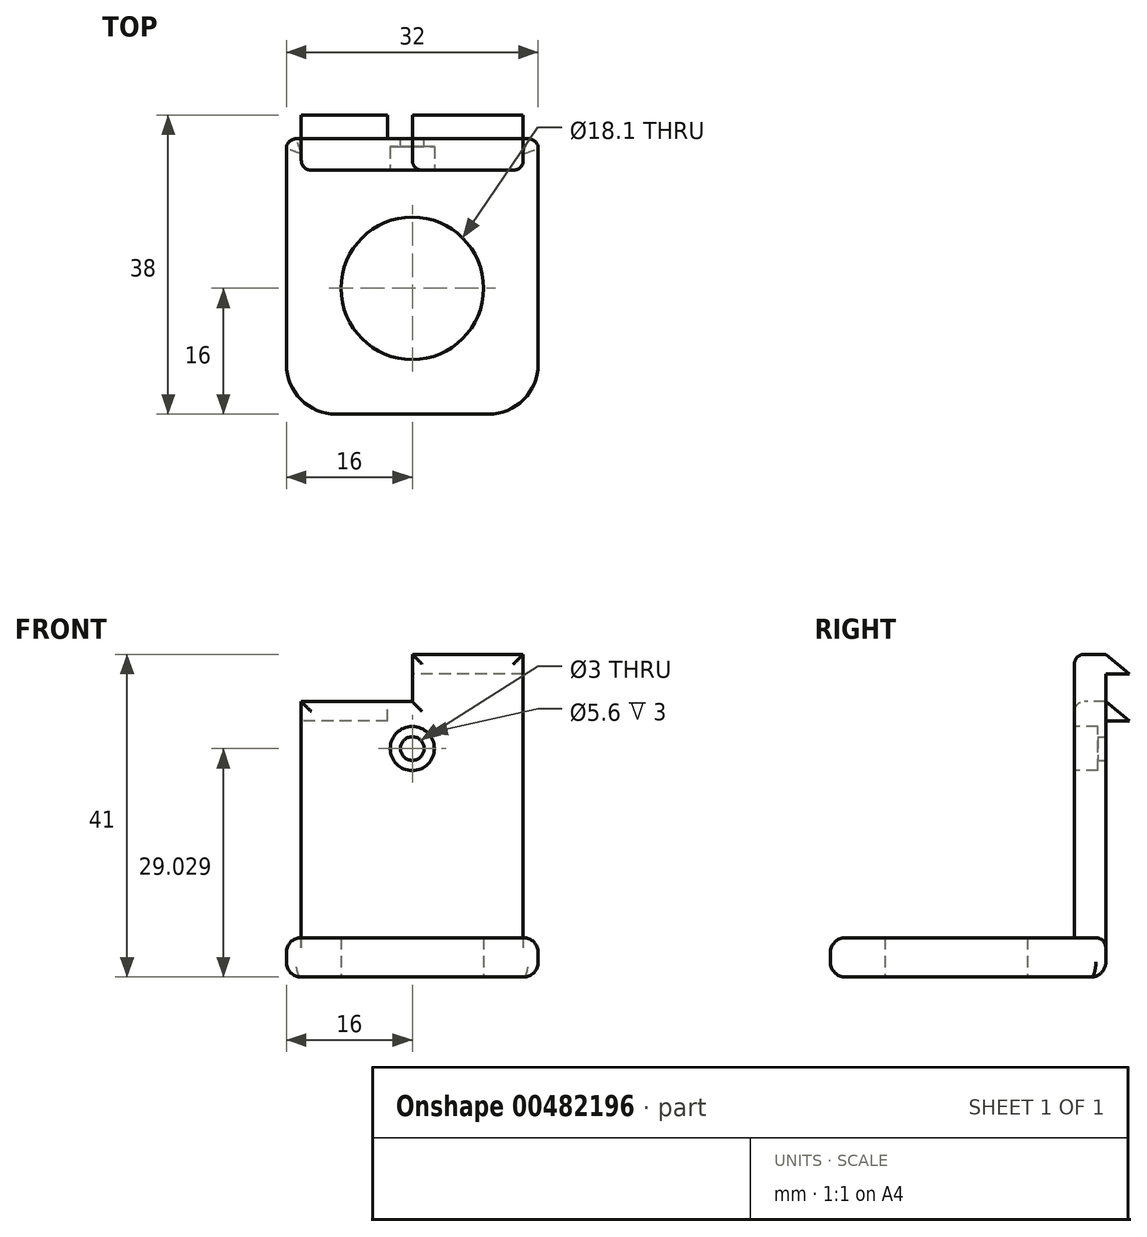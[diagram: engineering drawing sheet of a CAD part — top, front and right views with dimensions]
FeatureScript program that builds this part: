
annotation { "Feature Type Name" : "Feature", "Feature Type Description" : "" }
export const myFeature = defineFeature(function(context is Context, id is Id, definition is map)
    precondition{}
    {
        {
            var Q0;
            Q0=qCreatedBy(makeId("Top.planeOp"),FACE);
            var sketch = newSketch(context, id + "F0", { "sketchPlane" : qUnion([Q0])});
            skCircle(sketch, "E0", {"center": v(0, 0) * mm, "radius": 9.05 * mm});
            skLineSegment(sketch, "E1.bottom", {"start": v(-16, 19) * mm, "end": v(16, 19) * mm});
            skLineSegment(sketch, "E1.top", {"start": v(-9.65, -16) * mm, "end": v(9.65, -16) * mm});
            skLineSegment(sketch, "E1.left", {"start": v(-16, 19) * mm, "end": v(-16, -9.65) * mm});
            skLineSegment(sketch, "E1.right", {"start": v(16, 19) * mm, "end": v(16, -9.65) * mm});
            skPoint(sketch, "E2.visualSharp", {"position": v(-16, -16) * mm});
            skArc(sketch, "E2.filletArc", {"start": v(-16, -9.65) * mm, "mid": v(-14.14, -14.14) * mm, "end": v(-9.65, -16) * mm});
            skPoint(sketch, "E3.visualSharp", {"position": v(16, -16) * mm});
            skArc(sketch, "E3.filletArc", {"start": v(9.65, -16) * mm, "mid": v(14.14, -14.14) * mm, "end": v(16, -9.65) * mm});
            skSolve(sketch);
        }
        {
            var Q0;
            Q0=makeQuery(id+"F0.imprint","IMPRINT",FACE,{"disambiguationData":[TD([[makeQuery(id+"F0.imprint","IMPRINT",EDGE,{"derivedFrom":sQuery(id+"F0.wireOp",EDGE,"E0")}),-1.0]])]});
            extrude(context, id + "F1", {"entities" : qUnion([Q0]), "depth" : 5 * mm});
        }
        {
            var Q0;
            Q0=makeQuery(id+"F1.opExtrude","CAP_EDGE",EDGE,{"disambiguationData":[OSD([sQuery(id+"F0.wireOp",EDGE,"E1.bottom")])],"isStart":true});
            var Q1;
            Q1=makeQuery(id+"F1.opExtrude","CAP_EDGE",EDGE,{"disambiguationData":[OSD([sQuery(id+"F0.wireOp",EDGE,"E1.right")])],"isStart":true});
            fillet(context, id + "F2", {"entities" : qUnion([Q0, Q1]), "radius" : 1.9 * mm, "tangentPropagation" : true, "allowEdgeOverflow" : false});
        }
        {
            var Q0;
            Q0=makeQuery(id+"F1.opExtrude","CAP_EDGE",EDGE,{"disambiguationData":[OSD([sQuery(id+"F0.wireOp",EDGE,"E1.top")])],"isStart":false});
            var Q1;
            Q1=makeQuery(id+"F1.opExtrude","CAP_EDGE",EDGE,{"disambiguationData":[OSD([sQuery(id+"F0.wireOp",EDGE,"E1.right")])],"isStart":false});
            fillet(context, id + "F3", {"entities" : qUnion([Q0, Q1]), "radius" : 1.9 * mm, "tangentPropagation" : true, "allowEdgeOverflow" : false});
        }
        {
            var Q0;
            Q0=makeQuery(id+"F1.opExtrude","CAP_FACE",FACE,{"disambiguationData":[OSD([sQuery(id+"F0.wireOp",EDGE,"E0"),sQuery(id+"F0.wireOp",EDGE,"E1.bottom"),sQuery(id+"F0.wireOp",EDGE,"E1.top"),sQuery(id+"F0.wireOp",EDGE,"E1.left"),sQuery(id+"F0.wireOp",EDGE,"E1.right"),sQuery(id+"F0.wireOp",EDGE,"E2.filletArc"),sQuery(id+"F0.wireOp",EDGE,"E3.filletArc")])],"isStart":false});
            var sketch = newSketch(context, id + "F4", { "sketchPlane" : qUnion([Q0])});
            skLineSegment(sketch, "E4.bottom", {"start": v(-14.1, 19) * mm, "end": v(14.1, 19) * mm});
            skLineSegment(sketch, "E4.top", {"start": v(-14.1, 15) * mm, "end": v(14.1, 15) * mm});
            skLineSegment(sketch, "E4.left", {"start": v(-14.1, 19) * mm, "end": v(-14.1, 15) * mm});
            skLineSegment(sketch, "E4.right", {"start": v(14.1, 19) * mm, "end": v(14.1, 15) * mm});
            skSolve(sketch);
        }
        {
            var Q0;
            Q0=makeQuery(id+"F4.imprint","IMPRINT",FACE,{"disambiguationData":[TD([[makeQuery(id+"F4.imprint","IMPRINT",EDGE,{"derivedFrom":sQuery(id+"F4.wireOp",EDGE,"E4.bottom")}),-1.0]])]});
            extrude(context, id + "F5", {"entities" : qUnion([Q0]), "operationType" : NewBodyOperationType.ADD, "depth" : 30 * mm});
        }
        {
            var Q0;
            Q0=qCreatedBy(makeId("Right.planeOp"),FACE);
            var sketch = newSketch(context, id + "F6", { "sketchPlane" : qUnion([Q0])});
            skLineSegment(sketch, "E5", {"start": v(19, 35) * mm, "end": v(19, 32.53) * mm});
            skLineSegment(sketch, "E6", {"start": v(19, 32.53) * mm, "end": v(22, 32.53) * mm});
            skLineSegment(sketch, "E7", {"start": v(22, 32.53) * mm, "end": v(19, 35) * mm});
            skSolve(sketch);
        }
        {
            var Q0;
            Q0=makeQuery(id+"F6.imprint","IMPRINT",FACE,{"disambiguationData":[TD([[makeQuery(id+"F6.imprint","IMPRINT",EDGE,{"derivedFrom":sQuery(id+"F6.wireOp",EDGE,"E5")}),1.0]])]});
            var Q1;
            Q1=makeQuery(id+"F5.opExtrude","SWEPT_FACE",FACE,{"disambiguationData":[OSD([sQuery(id+"F4.wireOp",EDGE,"E4.right")])]});
            var Q2;
            Q2=makeQuery(id+"F5.opExtrude","SWEPT_FACE",FACE,{"disambiguationData":[OSD([sQuery(id+"F4.wireOp",EDGE,"E4.left")])]});
            extrude(context, id + "F7", {"entities" : qUnion([Q0]), "operationType" : NewBodyOperationType.ADD, "endBound" : BoundingType.UP_TO_SURFACE, "endBoundEntityFace" : qUnion([Q1]), "depth" : 25.4 * mm, "hasSecondDirection" : true, "secondDirectionBound" : SecondDirectionBoundingType.UP_TO_SURFACE, "secondDirectionOppositeDirection" : true, "secondDirectionBoundEntityFace" : qUnion([Q2]), "secondDirectionDepth" : 25.4 * mm});
        }
        {
            var Q0;
            Q0=makeQuery(id+"F5.boolean.opBoolean","MERGE",FACE,{"derivedFrom":[makeQuery(id+"F1.opExtrude","SWEPT_FACE",FACE,{"disambiguationData":[OSD([sQuery(id+"F0.wireOp",EDGE,"E1.bottom")])]}),makeQuery(id+"F5.opExtrude","SWEPT_FACE",FACE,{"disambiguationData":[OSD([sQuery(id+"F4.wireOp",EDGE,"E4.bottom")])]})]});
            var sketch = newSketch(context, id + "F8", { "sketchPlane" : qUnion([Q0])});
            skCircle(sketch, "E8", {"center": v(0, 29.03) * mm, "radius": 1.5 * mm});
            skSolve(sketch);
        }
        {
            var Q0;
            Q0=makeQuery(id+"F8.imprint","IMPRINT",FACE,{"disambiguationData":[TD([[makeQuery(id+"F8.imprint","IMPRINT",EDGE,{"derivedFrom":sQuery(id+"F8.wireOp",EDGE,"E8")}),1.0]])]});
            var Q1;
            Q1=makeQuery(id+"F5.opExtrude","SWEPT_FACE",FACE,{"disambiguationData":[OSD([sQuery(id+"F4.wireOp",EDGE,"E4.top")])]});
            extrude(context, id + "F9", {"entities" : qUnion([Q0]), "operationType" : NewBodyOperationType.REMOVE, "endBound" : BoundingType.UP_TO_SURFACE, "oppositeDirection" : true, "endBoundEntityFace" : qUnion([Q1]), "depth" : 25.4 * mm});
        }
        {
            var Q0;
            Q0=makeQuery(id+"F5.opExtrude","SWEPT_FACE",FACE,{"disambiguationData":[OSD([sQuery(id+"F4.wireOp",EDGE,"E4.top")])]});
            var sketch = newSketch(context, id + "F10", { "sketchPlane" : qUnion([Q0])});
            skCircle(sketch, "E9", {"center": v(0, 29.03) * mm, "radius": 2.8 * mm});
            skSolve(sketch);
        }
        {
            var Q0;
            Q0=makeQuery(id+"F10.imprint","IMPRINT",FACE,{"disambiguationData":[TD([[makeQuery(id+"F10.imprint","IMPRINT",EDGE,{"derivedFrom":sQuery(id+"F10.wireOp",EDGE,"E9")}),1.0]])]});
            extrude(context, id + "F11", {"entities" : qUnion([Q0]), "operationType" : NewBodyOperationType.REMOVE, "oppositeDirection" : true, "depth" : 3 * mm});
        }
        {
            var Q0;
            Q0=qCreatedBy(makeId("Right.planeOp"),FACE);
            var sketch = newSketch(context, id + "F12", { "sketchPlane" : qUnion([Q0])});
            skLineSegment(sketch, "E10", {"start": v(19, 30.98) * mm, "end": v(19, 35) * mm});
            skLineSegment(sketch, "E11", {"start": v(19, 35) * mm, "end": v(23.3, 32.12) * mm});
            skLineSegment(sketch, "E12", {"start": v(23.3, 32.12) * mm, "end": v(19, 30.98) * mm});
            skSolve(sketch);
        }
        {
            var Q0;
            Q0=makeQuery(id+"F12.imprint","IMPRINT",FACE,{"disambiguationData":[TD([[makeQuery(id+"F12.imprint","IMPRINT",EDGE,{"derivedFrom":sQuery(id+"F12.wireOp",EDGE,"E10")}),-1.0]])]});
            extrude(context, id + "F13", {"entities" : qUnion([Q0]), "operationType" : NewBodyOperationType.REMOVE, "depth" : 14.82 * mm, "hasSecondDirection" : true, "secondDirectionOppositeDirection" : true, "secondDirectionDepth" : 3.12 * mm});
        }
        {
            var Q0;
            Q0=makeQuery(id+"F5.opExtrude","CAP_FACE",FACE,{"disambiguationData":[OSD([sQuery(id+"F4.wireOp",EDGE,"E4.bottom"),sQuery(id+"F4.wireOp",EDGE,"E4.top"),sQuery(id+"F4.wireOp",EDGE,"E4.left"),sQuery(id+"F4.wireOp",EDGE,"E4.right")])],"isStart":false});
            var sketch = newSketch(context, id + "F14", { "sketchPlane" : qUnion([Q0])});
            skLineSegment(sketch, "E13.bottom", {"start": v(0, 19) * mm, "end": v(14.1, 19) * mm});
            skLineSegment(sketch, "E13.top", {"start": v(0, 15) * mm, "end": v(14.1, 15) * mm});
            skLineSegment(sketch, "E13.left", {"start": v(0, 19) * mm, "end": v(0, 15) * mm});
            skLineSegment(sketch, "E13.right", {"start": v(14.1, 19) * mm, "end": v(14.1, 15) * mm});
            skSolve(sketch);
        }
        {
            var Q0;
            Q0=qSketchRegion(id+"F14",true);
            extrude(context, id + "F15", {"entities" : qUnion([Q0]), "operationType" : NewBodyOperationType.ADD, "depth" : 6 * mm});
        }
        {
            var Q0;
            Q0=qCreatedBy(makeId("Right.planeOp"),FACE);
            var sketch = newSketch(context, id + "F16", { "sketchPlane" : qUnion([Q0])});
            skLineSegment(sketch, "E14", {"start": v(19, 41) * mm, "end": v(22, 38.53) * mm});
            skLineSegment(sketch, "E15", {"start": v(22, 38.53) * mm, "end": v(19, 38.53) * mm});
            skLineSegment(sketch, "E16", {"start": v(19, 38.53) * mm, "end": v(19, 41) * mm});
            skSolve(sketch);
        }
        {
            var Q0;
            Q0=makeQuery(id+"F16.imprint","IMPRINT",FACE,{"disambiguationData":[TD([[makeQuery(id+"F16.imprint","IMPRINT",EDGE,{"derivedFrom":sQuery(id+"F16.wireOp",EDGE,"E14")}),-1.0]])]});
            var Q1;
            Q1=makeQuery(id+"F15.boolean.opBoolean","MERGE",FACE,{"derivedFrom":[makeQuery(id+"F7.boolean.opBoolean","MERGE",FACE,{"derivedFrom":[makeQuery(id+"F5.opExtrude","SWEPT_FACE",FACE,{"disambiguationData":[OSD([sQuery(id+"F4.wireOp",EDGE,"E4.right")])]}),makeQuery(id+"F7.opExtrude","CAP_FACE",FACE,{"disambiguationData":[OSD([sQuery(id+"F6.wireOp",EDGE,"E5"),sQuery(id+"F6.wireOp",EDGE,"E6"),sQuery(id+"F6.wireOp",EDGE,"E7")])],"isStart":false})]}),makeQuery(id+"F15.opExtrude","SWEPT_FACE",FACE,{"disambiguationData":[OSD([sQuery(id+"F14.wireOp",EDGE,"E13.right")])]})]});
            extrude(context, id + "F17", {"entities" : qUnion([Q0]), "operationType" : NewBodyOperationType.ADD, "endBound" : BoundingType.UP_TO_SURFACE, "endBoundEntityFace" : qUnion([Q1]), "depth" : 25.4 * mm});
        }
        {
            var Q0;
            Q0=makeQuery(id+"F5.opExtrude","SWEPT_EDGE",EDGE,{"disambiguationData":[OSD([sQuery(id+"F0.wireOp",EDGE,"E0"),sQuery(id+"F0.wireOp",EDGE,"E1.bottom"),sQuery(id+"F0.wireOp",EDGE,"E1.top"),sQuery(id+"F0.wireOp",EDGE,"E1.left"),sQuery(id+"F0.wireOp",EDGE,"E1.right"),sQuery(id+"F0.wireOp",EDGE,"E2.filletArc"),sQuery(id+"F0.wireOp",EDGE,"E3.filletArc"),sQuery(id+"F4.wireOp",EDGE,"E4.top"),sQuery(id+"F4.wireOp",EDGE,"E4.right")])]});
            var Q1;
            Q1=makeQuery(id+"F15.boolean.opBoolean","MERGE",EDGE,{"derivedFrom":[makeQuery(id+"F5.opExtrude","SWEPT_EDGE",EDGE,{"disambiguationData":[OSD([sQuery(id+"F0.wireOp",EDGE,"E0"),sQuery(id+"F0.wireOp",EDGE,"E1.bottom"),sQuery(id+"F0.wireOp",EDGE,"E1.top"),sQuery(id+"F0.wireOp",EDGE,"E1.left"),sQuery(id+"F0.wireOp",EDGE,"E1.right"),sQuery(id+"F0.wireOp",EDGE,"E2.filletArc"),sQuery(id+"F0.wireOp",EDGE,"E3.filletArc"),sQuery(id+"F4.wireOp",EDGE,"E4.top"),sQuery(id+"F4.wireOp",EDGE,"E4.left")])]}),makeQuery(id+"F15.opExtrude","SWEPT_EDGE",EDGE,{"disambiguationData":[OSD([sQuery(id+"F14.wireOp",EDGE,"9835426e-c448-4567-998b-7149fbf15287.bottom"),sQuery(id+"F14.wireOp",EDGE,"9835426e-c448-4567-998b-7149fbf15287.right")])]})]});
            var Q2;
            Q2=makeQuery(id+"F15.opExtrude","CAP_EDGE",EDGE,{"disambiguationData":[OSD([sQuery(id+"F14.wireOp",EDGE,"9835426e-c448-4567-998b-7149fbf15287.bottom")])],"isStart":false});
            var Q3;
            Q3=makeQuery(id+"F5.opExtrude","CAP_EDGE",EDGE,{"disambiguationData":[OSD([sQuery(id+"F4.wireOp",EDGE,"E4.top")])],"isStart":false});
            var Q4;
            Q4=makeQuery(id+"F15.opExtrude","SWEPT_EDGE",EDGE,{"disambiguationData":[OSD([sQuery(id+"F4.wireOp",EDGE,"E4.top"),sQuery(id+"F14.wireOp",EDGE,"9835426e-c448-4567-998b-7149fbf15287.bottom"),sQuery(id+"F14.wireOp",EDGE,"9835426e-c448-4567-998b-7149fbf15287.right")])]});
            var Q5;
            Q5=makeQuery(id+"F5.opExtrude","SWEPT_EDGE",EDGE,{"disambiguationData":[OSD([sQuery(id+"F0.wireOp",EDGE,"E0"),sQuery(id+"F0.wireOp",EDGE,"E1.bottom"),sQuery(id+"F0.wireOp",EDGE,"E1.top"),sQuery(id+"F0.wireOp",EDGE,"E1.left"),sQuery(id+"F0.wireOp",EDGE,"E1.right"),sQuery(id+"F0.wireOp",EDGE,"E2.filletArc"),sQuery(id+"F0.wireOp",EDGE,"E3.filletArc"),sQuery(id+"F4.wireOp",EDGE,"E4.top"),sQuery(id+"F4.wireOp",EDGE,"E4.left")])]});
            var Q6;
            Q6=makeQuery(id+"F15.opExtrude","CAP_EDGE",EDGE,{"disambiguationData":[OSD([sQuery(id+"F14.wireOp",EDGE,"E13.top")])],"isStart":false});
            fillet(context, id + "F18", {"entities" : qUnion([Q0, Q1, Q2, Q3, Q4, Q5, Q6]), "radius" : 1.27 * mm, "tangentPropagation" : true, "allowEdgeOverflow" : false});
        }
        {
            var Q0;
            Q0=makeQuery(id+"F1.opExtrude","SWEPT_EDGE",EDGE,{"disambiguationData":[OSD([sQuery(id+"F0.wireOp",EDGE,"E1.bottom"),sQuery(id+"F0.wireOp",EDGE,"E1.left")])]});
            var Q1;
            Q1=makeQuery(id+"F1.opExtrude","SWEPT_EDGE",EDGE,{"disambiguationData":[OSD([sQuery(id+"F0.wireOp",EDGE,"E1.bottom"),sQuery(id+"F0.wireOp",EDGE,"E1.right")])]});
            fillet(context, id + "F19", {"entities" : qUnion([Q0, Q1]), "radius" : 1.27 * mm, "tangentPropagation" : true, "allowEdgeOverflow" : false});
        }
    });
